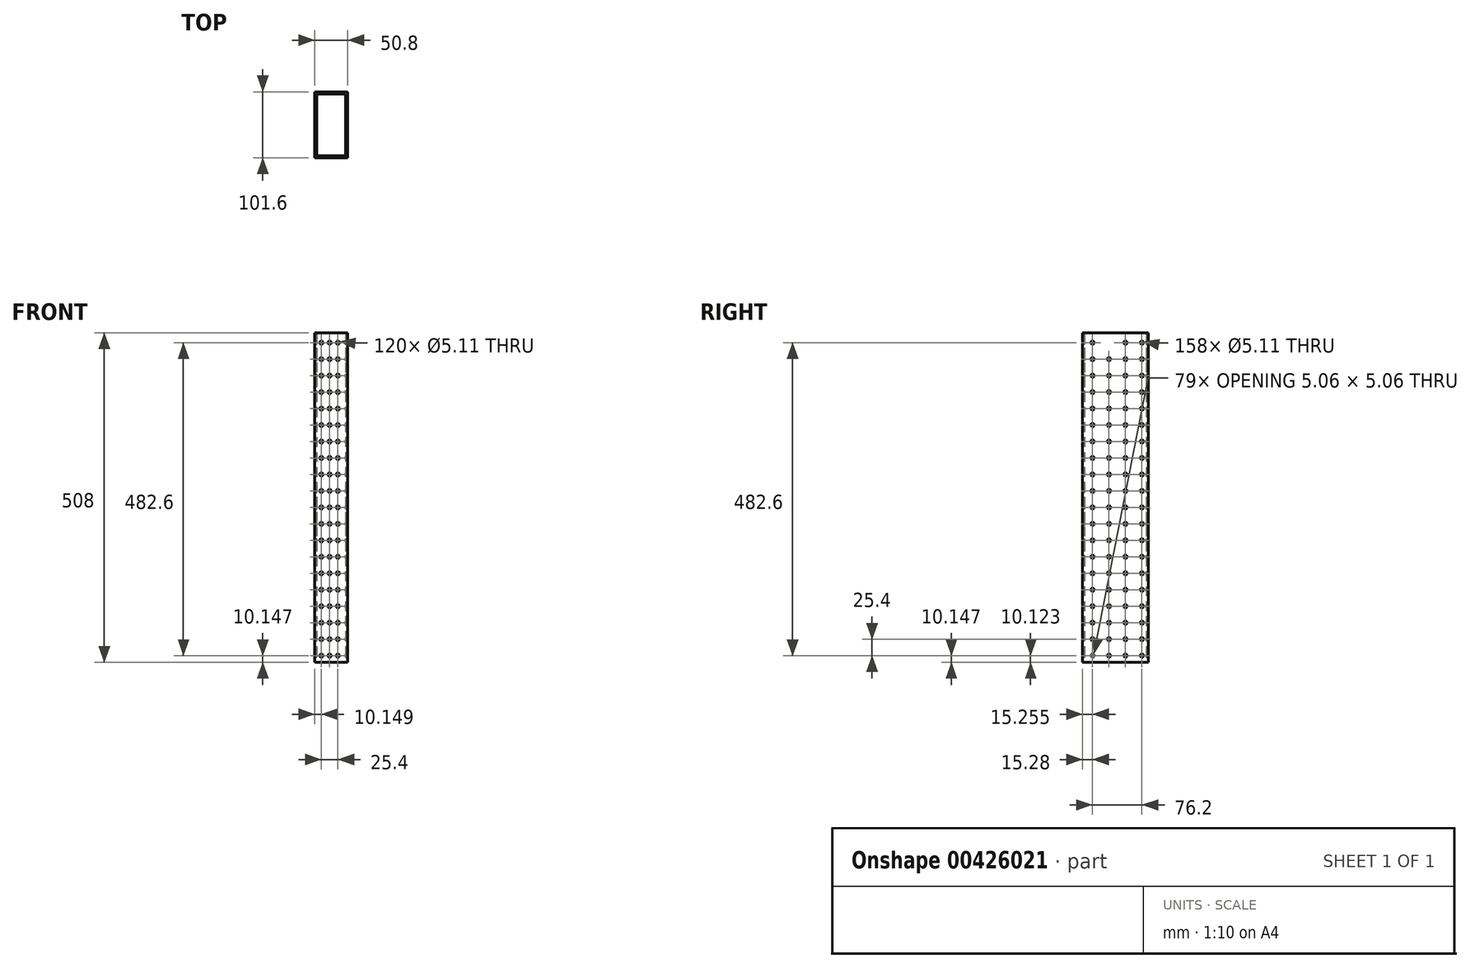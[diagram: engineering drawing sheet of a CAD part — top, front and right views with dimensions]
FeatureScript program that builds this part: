
annotation { "Feature Type Name" : "Feature", "Feature Type Description" : "" }
export const myFeature = defineFeature(function(context is Context, id is Id, definition is map)
    precondition{}
    {
        {
            var Q0;
            Q0=qCreatedBy(makeId("Top.planeOp"),FACE);
            var sketch = newSketch(context, id + "F0", { "sketchPlane" : qUnion([Q0])});
            skLineSegment(sketch, "E0.bottom", {"start": v(-26.2, 70.95) * mm, "end": v(24.6, 70.95) * mm});
            skLineSegment(sketch, "E0.top", {"start": v(-26.2, -30.65) * mm, "end": v(24.6, -30.65) * mm});
            skLineSegment(sketch, "E0.left", {"start": v(-26.2, 70.95) * mm, "end": v(-26.2, -30.65) * mm});
            skLineSegment(sketch, "E0.right", {"start": v(24.6, 70.95) * mm, "end": v(24.6, -30.65) * mm});
            skLineSegment(sketch, "E1.bottom", {"start": v(21.42, 67.78) * mm, "end": v(-23.03, 67.78) * mm});
            skLineSegment(sketch, "E1.top", {"start": v(21.42, -27.47) * mm, "end": v(-23.03, -27.47) * mm});
            skLineSegment(sketch, "E1.left", {"start": v(21.42, 67.78) * mm, "end": v(21.42, -27.47) * mm});
            skLineSegment(sketch, "E1.right", {"start": v(-23.03, 67.78) * mm, "end": v(-23.03, -27.47) * mm});
            skSolve(sketch);
        }
        {
            var Q0;
            Q0 = qSketchRegion(id + "F0", true);
            extrude(context, id + "F1", {"entities" : qUnion([Q0]), "depth" : 508 * mm});
        }
        {
            var Q0;
            Q0=makeQuery(id+"F1.opExtrude","SWEPT_FACE",FACE,{"disambiguationData":[OSD([sQuery(id+"F0.wireOp",EDGE,"E0.right")])]});
            var sketch = newSketch(context, id + "F2", { "sketchPlane" : qUnion([Q0])});
            skCircle(sketch, "E2", {"center": v(-15.4, 492.75) * mm, "radius": 2.55 * mm});
            skCircle(sketch, "E3.1.0.0", {"center": v(10, 492.75) * mm, "radius": 2.55 * mm});
            skCircle(sketch, "E3.2.0.0", {"center": v(35.4, 492.75) * mm, "radius": 2.55 * mm});
            skCircle(sketch, "E3.3.0.0", {"center": v(60.8, 492.75) * mm, "radius": 2.55 * mm});
            skLineSegment(sketch, "E3.direction1", {"start": v(-15.4, 492.75) * mm, "end": v(10, 492.75) * mm, "construction": true});
            skCircle(sketch, "E4.0.1.0", {"center": v(-15.4, 467.35) * mm, "radius": 2.55 * mm});
            skCircle(sketch, "E4.0.2.0", {"center": v(-15.4, 441.95) * mm, "radius": 2.55 * mm});
            skCircle(sketch, "E4.0.3.0", {"center": v(-15.4, 416.55) * mm, "radius": 2.55 * mm});
            skCircle(sketch, "E4.0.4.0", {"center": v(-15.4, 391.15) * mm, "radius": 2.55 * mm});
            skCircle(sketch, "E4.0.5.0", {"center": v(-15.4, 365.75) * mm, "radius": 2.55 * mm});
            skCircle(sketch, "E4.0.6.0", {"center": v(-15.4, 340.35) * mm, "radius": 2.55 * mm});
            skCircle(sketch, "E4.0.7.0", {"center": v(-15.4, 314.95) * mm, "radius": 2.55 * mm});
            skCircle(sketch, "E4.0.8.0", {"center": v(-15.4, 289.55) * mm, "radius": 2.55 * mm});
            skCircle(sketch, "E4.0.9.0", {"center": v(-15.4, 264.15) * mm, "radius": 2.55 * mm});
            skCircle(sketch, "E4.0.10.0", {"center": v(-15.4, 238.75) * mm, "radius": 2.55 * mm});
            skCircle(sketch, "E4.0.11.0", {"center": v(-15.4, 213.35) * mm, "radius": 2.55 * mm});
            skCircle(sketch, "E4.0.12.0", {"center": v(-15.4, 187.95) * mm, "radius": 2.55 * mm});
            skCircle(sketch, "E4.0.13.0", {"center": v(-15.4, 162.55) * mm, "radius": 2.55 * mm});
            skCircle(sketch, "E4.0.14.0", {"center": v(-15.4, 137.15) * mm, "radius": 2.55 * mm});
            skCircle(sketch, "E4.0.15.0", {"center": v(-15.4, 111.75) * mm, "radius": 2.55 * mm});
            skCircle(sketch, "E4.0.16.0", {"center": v(-15.4, 86.35) * mm, "radius": 2.55 * mm});
            skCircle(sketch, "E4.0.17.0", {"center": v(-15.4, 60.95) * mm, "radius": 2.55 * mm});
            skCircle(sketch, "E4.0.18.0", {"center": v(-15.4, 35.55) * mm, "radius": 2.55 * mm});
            skCircle(sketch, "E4.0.19.0", {"center": v(-15.4, 10.15) * mm, "radius": 2.55 * mm});
            skCircle(sketch, "E4.1.1.0", {"center": v(10, 467.35) * mm, "radius": 2.55 * mm});
            skCircle(sketch, "E4.1.2.0", {"center": v(10, 441.95) * mm, "radius": 2.55 * mm});
            skCircle(sketch, "E4.1.3.0", {"center": v(10, 416.55) * mm, "radius": 2.55 * mm});
            skCircle(sketch, "E4.1.4.0", {"center": v(10, 391.15) * mm, "radius": 2.55 * mm});
            skCircle(sketch, "E4.1.5.0", {"center": v(10, 365.75) * mm, "radius": 2.55 * mm});
            skCircle(sketch, "E4.1.6.0", {"center": v(10, 340.35) * mm, "radius": 2.55 * mm});
            skCircle(sketch, "E4.1.7.0", {"center": v(10, 314.95) * mm, "radius": 2.55 * mm});
            skCircle(sketch, "E4.1.8.0", {"center": v(10, 289.55) * mm, "radius": 2.55 * mm});
            skCircle(sketch, "E4.1.9.0", {"center": v(10, 264.15) * mm, "radius": 2.55 * mm});
            skCircle(sketch, "E4.1.10.0", {"center": v(10, 238.75) * mm, "radius": 2.55 * mm});
            skCircle(sketch, "E4.1.11.0", {"center": v(10, 213.35) * mm, "radius": 2.55 * mm});
            skCircle(sketch, "E4.1.12.0", {"center": v(10, 187.95) * mm, "radius": 2.55 * mm});
            skCircle(sketch, "E4.1.13.0", {"center": v(10, 162.55) * mm, "radius": 2.55 * mm});
            skCircle(sketch, "E4.1.14.0", {"center": v(10, 137.15) * mm, "radius": 2.55 * mm});
            skCircle(sketch, "E4.1.15.0", {"center": v(10, 111.75) * mm, "radius": 2.55 * mm});
            skCircle(sketch, "E4.1.16.0", {"center": v(10, 86.35) * mm, "radius": 2.55 * mm});
            skCircle(sketch, "E4.1.17.0", {"center": v(10, 60.95) * mm, "radius": 2.55 * mm});
            skCircle(sketch, "E4.1.18.0", {"center": v(10, 35.55) * mm, "radius": 2.55 * mm});
            skCircle(sketch, "E4.1.19.0", {"center": v(10, 10.15) * mm, "radius": 2.55 * mm});
            skCircle(sketch, "E4.2.1.0", {"center": v(35.4, 467.35) * mm, "radius": 2.55 * mm});
            skCircle(sketch, "E4.2.2.0", {"center": v(35.4, 441.95) * mm, "radius": 2.55 * mm});
            skCircle(sketch, "E4.2.3.0", {"center": v(35.4, 416.55) * mm, "radius": 2.55 * mm});
            skCircle(sketch, "E4.2.4.0", {"center": v(35.4, 391.15) * mm, "radius": 2.55 * mm});
            skCircle(sketch, "E4.2.5.0", {"center": v(35.4, 365.75) * mm, "radius": 2.55 * mm});
            skCircle(sketch, "E4.2.6.0", {"center": v(35.4, 340.35) * mm, "radius": 2.55 * mm});
            skCircle(sketch, "E4.2.7.0", {"center": v(35.4, 314.95) * mm, "radius": 2.55 * mm});
            skCircle(sketch, "E4.2.8.0", {"center": v(35.4, 289.55) * mm, "radius": 2.55 * mm});
            skCircle(sketch, "E4.2.9.0", {"center": v(35.4, 264.15) * mm, "radius": 2.55 * mm});
            skCircle(sketch, "E4.2.10.0", {"center": v(35.4, 238.75) * mm, "radius": 2.55 * mm});
            skCircle(sketch, "E4.2.11.0", {"center": v(35.4, 213.35) * mm, "radius": 2.55 * mm});
            skCircle(sketch, "E4.2.12.0", {"center": v(35.4, 187.95) * mm, "radius": 2.55 * mm});
            skCircle(sketch, "E4.2.13.0", {"center": v(35.4, 162.55) * mm, "radius": 2.55 * mm});
            skCircle(sketch, "E4.2.14.0", {"center": v(35.4, 137.15) * mm, "radius": 2.55 * mm});
            skCircle(sketch, "E4.2.15.0", {"center": v(35.4, 111.75) * mm, "radius": 2.55 * mm});
            skCircle(sketch, "E4.2.16.0", {"center": v(35.4, 86.35) * mm, "radius": 2.55 * mm});
            skCircle(sketch, "E4.2.17.0", {"center": v(35.4, 60.95) * mm, "radius": 2.55 * mm});
            skCircle(sketch, "E4.2.18.0", {"center": v(35.4, 35.55) * mm, "radius": 2.55 * mm});
            skCircle(sketch, "E4.2.19.0", {"center": v(35.4, 10.15) * mm, "radius": 2.55 * mm});
            skLineSegment(sketch, "E4.direction2", {"start": v(-15.4, 492.75) * mm, "end": v(-15.4, 467.35) * mm, "construction": true});
            skCircle(sketch, "E5.0.3.1", {"center": v(60.8, 467.35) * mm, "radius": 2.55 * mm});
            skCircle(sketch, "E5.0.3.2", {"center": v(60.8, 441.95) * mm, "radius": 2.55 * mm});
            skCircle(sketch, "E5.0.3.3", {"center": v(60.8, 416.55) * mm, "radius": 2.55 * mm});
            skCircle(sketch, "E5.0.3.4", {"center": v(60.8, 391.15) * mm, "radius": 2.55 * mm});
            skCircle(sketch, "E5.0.3.5", {"center": v(60.8, 365.75) * mm, "radius": 2.55 * mm});
            skCircle(sketch, "E5.0.3.6", {"center": v(60.8, 340.35) * mm, "radius": 2.55 * mm});
            skCircle(sketch, "E5.0.3.7", {"center": v(60.8, 314.95) * mm, "radius": 2.55 * mm});
            skCircle(sketch, "E5.0.3.8", {"center": v(60.8, 289.55) * mm, "radius": 2.55 * mm});
            skCircle(sketch, "E5.0.3.9", {"center": v(60.8, 264.15) * mm, "radius": 2.55 * mm});
            skCircle(sketch, "E5.0.3.10", {"center": v(60.8, 238.75) * mm, "radius": 2.55 * mm});
            skCircle(sketch, "E5.0.3.11", {"center": v(60.8, 213.35) * mm, "radius": 2.55 * mm});
            skCircle(sketch, "E5.0.3.12", {"center": v(60.8, 187.95) * mm, "radius": 2.55 * mm});
            skCircle(sketch, "E5.0.3.13", {"center": v(60.8, 162.55) * mm, "radius": 2.55 * mm});
            skCircle(sketch, "E5.0.3.14", {"center": v(60.8, 137.15) * mm, "radius": 2.55 * mm});
            skCircle(sketch, "E5.0.3.15", {"center": v(60.8, 111.75) * mm, "radius": 2.55 * mm});
            skCircle(sketch, "E5.0.3.16", {"center": v(60.8, 86.35) * mm, "radius": 2.55 * mm});
            skCircle(sketch, "E5.0.3.17", {"center": v(60.8, 60.95) * mm, "radius": 2.55 * mm});
            skCircle(sketch, "E5.0.3.18", {"center": v(60.8, 35.55) * mm, "radius": 2.55 * mm});
            skCircle(sketch, "E5.0.3.19", {"center": v(60.8, 10.15) * mm, "radius": 2.55 * mm});
            skSolve(sketch);
        }
        {
            var Q0;
            Q0=sQuery(id+"F2.wireOp",VERTEX,"E4.1.18.0.center");
            var Q1;
            Q1=sQuery(id+"F2.wireOp",VERTEX,"E5.0.3.1.center");
            var Q2;
            Q2=sQuery(id+"F2.wireOp",VERTEX,"E5.0.3.17.center");
            var Q3;
            Q3=sQuery(id+"F2.wireOp",VERTEX,"E5.0.3.10.center");
            var Q4;
            Q4=sQuery(id+"F2.wireOp",VERTEX,"E4.1.2.0.center");
            var Q5;
            Q5=sQuery(id+"F2.wireOp",VERTEX,"E4.1.9.0.center");
            var Q6;
            Q6=sQuery(id+"F2.wireOp",VERTEX,"E4.2.5.0.center");
            var Q7;
            Q7=sQuery(id+"F2.wireOp",VERTEX,"E4.2.14.0.center");
            var Q8;
            Q8=sQuery(id+"F2.wireOp",VERTEX,"E4.0.7.0.center");
            var Q9;
            Q9=sQuery(id+"F2.wireOp",VERTEX,"E5.0.3.18.center");
            var Q10;
            Q10=sQuery(id+"F2.wireOp",VERTEX,"E5.0.3.2.center");
            var Q11;
            Q11=sQuery(id+"F2.wireOp",VERTEX,"E5.0.3.11.center");
            var Q12;
            Q12=sQuery(id+"F2.wireOp",VERTEX,"E4.2.15.0.center");
            var Q13;
            Q13=sQuery(id+"F2.wireOp",VERTEX,"E4.1.19.0.center");
            var Q14;
            Q14=sQuery(id+"F2.wireOp",VERTEX,"E4.1.3.0.center");
            var Q15;
            Q15=sQuery(id+"F2.wireOp",VERTEX,"E4.2.6.0.center");
            var Q16;
            Q16=sQuery(id+"F2.wireOp",VERTEX,"E4.1.10.0.center");
            var Q17;
            Q17=sQuery(id+"F2.wireOp",VERTEX,"E4.0.14.0.center");
            var Q18;
            Q18=sQuery(id+"F2.wireOp",VERTEX,"E4.0.8.0.center");
            var Q19;
            Q19=sQuery(id+"F2.wireOp",VERTEX,"E5.0.3.12.center");
            var Q20;
            Q20=sQuery(id+"F2.wireOp",VERTEX,"E4.2.16.0.center");
            var Q21;
            Q21=sQuery(id+"F2.wireOp",VERTEX,"E4.1.4.0.center");
            var Q22;
            Q22=sQuery(id+"F2.wireOp",VERTEX,"E4.2.7.0.center");
            var Q23;
            Q23=sQuery(id+"F2.wireOp",VERTEX,"E4.1.11.0.center");
            var Q24;
            Q24=sQuery(id+"F2.wireOp",VERTEX,"E4.0.15.0.center");
            var Q25;
            Q25=sQuery(id+"F2.wireOp",VERTEX,"E5.0.3.19.center");
            var Q26;
            Q26=sQuery(id+"F2.wireOp",VERTEX,"E5.0.3.3.center");
            var Q27;
            Q27=sQuery(id+"F2.wireOp",VERTEX,"E4.0.4.0.center");
            var Q28;
            Q28=sQuery(id+"F2.wireOp",VERTEX,"E4.0.9.0.center");
            var Q29;
            Q29=sQuery(id+"F2.wireOp",VERTEX,"E4.0.5.0.center");
            var Q30;
            Q30=sQuery(id+"F2.wireOp",VERTEX,"E5.0.3.13.center");
            var Q31;
            Q31=sQuery(id+"F2.wireOp",VERTEX,"E4.0.6.0.center");
            var Q32;
            Q32=sQuery(id+"F2.wireOp",VERTEX,"E4.2.17.0.center");
            var Q33;
            Q33=sQuery(id+"F2.wireOp",VERTEX,"E4.2.1.0.center");
            var Q34;
            Q34=sQuery(id+"F2.wireOp",VERTEX,"E4.1.5.0.center");
            var Q35;
            Q35=sQuery(id+"F2.wireOp",VERTEX,"E2.center");
            var Q36;
            Q36=sQuery(id+"F2.wireOp",VERTEX,"E3.2.0.0.center");
            var Q37;
            Q37=sQuery(id+"F2.wireOp",VERTEX,"E3.3.0.0.center");
            var Q38;
            Q38=sQuery(id+"F2.wireOp",VERTEX,"E4.0.1.0.center");
            var Q39;
            Q39=sQuery(id+"F2.wireOp",VERTEX,"E4.0.2.0.center");
            var Q40;
            Q40=sQuery(id+"F2.wireOp",VERTEX,"E4.0.3.0.center");
            var Q41;
            Q41=sQuery(id+"F2.wireOp",VERTEX,"E4.2.8.0.center");
            var Q42;
            Q42=sQuery(id+"F2.wireOp",VERTEX,"E4.1.12.0.center");
            var Q43;
            Q43=sQuery(id+"F2.wireOp",VERTEX,"E4.0.16.0.center");
            var Q44;
            Q44=sQuery(id+"F2.wireOp",VERTEX,"E5.0.3.4.center");
            var Q45;
            Q45=sQuery(id+"F2.wireOp",VERTEX,"E4.0.10.0.center");
            var Q46;
            Q46=sQuery(id+"F2.wireOp",VERTEX,"E5.0.3.14.center");
            var Q47;
            Q47=sQuery(id+"F2.wireOp",VERTEX,"E4.2.18.0.center");
            var Q48;
            Q48=sQuery(id+"F2.wireOp",VERTEX,"E4.2.2.0.center");
            var Q49;
            Q49=sQuery(id+"F2.wireOp",VERTEX,"E4.1.6.0.center");
            var Q50;
            Q50=sQuery(id+"F2.wireOp",VERTEX,"E4.2.9.0.center");
            var Q51;
            Q51=sQuery(id+"F2.wireOp",VERTEX,"E4.1.13.0.center");
            var Q52;
            Q52=sQuery(id+"F2.wireOp",VERTEX,"E4.0.17.0.center");
            var Q53;
            Q53=sQuery(id+"F2.wireOp",VERTEX,"E5.0.3.5.center");
            var Q54;
            Q54=sQuery(id+"F2.wireOp",VERTEX,"E4.0.11.0.center");
            var Q55;
            Q55=sQuery(id+"F2.wireOp",VERTEX,"E5.0.3.15.center");
            var Q56;
            Q56=sQuery(id+"F2.wireOp",VERTEX,"E5.0.3.8.center");
            var Q57;
            Q57=sQuery(id+"F2.wireOp",VERTEX,"E4.2.19.0.center");
            var Q58;
            Q58=sQuery(id+"F2.wireOp",VERTEX,"E4.2.12.0.center");
            var Q59;
            Q59=sQuery(id+"F2.wireOp",VERTEX,"E4.1.16.0.center");
            var Q60;
            Q60=sQuery(id+"F2.wireOp",VERTEX,"E4.2.3.0.center");
            var Q61;
            Q61=sQuery(id+"F2.wireOp",VERTEX,"E3.1.0.0.center");
            var Q62;
            Q62=sQuery(id+"F2.wireOp",VERTEX,"E4.1.7.0.center");
            var Q63;
            Q63=sQuery(id+"F2.wireOp",VERTEX,"E4.0.13.0.center");
            var Q64;
            Q64=sQuery(id+"F2.wireOp",VERTEX,"E5.0.3.7.center");
            var Q65;
            Q65=sQuery(id+"F2.wireOp",VERTEX,"E4.0.19.0.center");
            var Q66;
            Q66=sQuery(id+"F2.wireOp",VERTEX,"E4.1.15.0.center");
            var Q67;
            Q67=sQuery(id+"F2.wireOp",VERTEX,"E4.2.11.0.center");
            var Q68;
            Q68=sQuery(id+"F2.wireOp",VERTEX,"E4.1.1.0.center");
            var Q69;
            Q69=sQuery(id+"F2.wireOp",VERTEX,"E4.1.8.0.center");
            var Q70;
            Q70=sQuery(id+"F2.wireOp",VERTEX,"E4.1.17.0.center");
            var Q71;
            Q71=sQuery(id+"F2.wireOp",VERTEX,"E4.2.4.0.center");
            var Q72;
            Q72=sQuery(id+"F2.wireOp",VERTEX,"E4.2.13.0.center");
            var Q73;
            Q73=sQuery(id+"F2.wireOp",VERTEX,"E5.0.3.9.center");
            var Q74;
            Q74=sQuery(id+"F2.wireOp",VERTEX,"E5.0.3.16.center");
            var Q75;
            Q75=sQuery(id+"F2.wireOp",VERTEX,"E4.0.12.0.center");
            var Q76;
            Q76=sQuery(id+"F2.wireOp",VERTEX,"E5.0.3.6.center");
            var Q77;
            Q77=sQuery(id+"F2.wireOp",VERTEX,"E4.0.18.0.center");
            var Q78;
            Q78=sQuery(id+"F2.wireOp",VERTEX,"E4.1.14.0.center");
            var Q79;
            Q79=sQuery(id+"F2.wireOp",VERTEX,"E4.2.10.0.center");
            var Q80;
            Q80=makeQuery(id+"F1.opExtrude","SWEPT_BODY",BODY,{"disambiguationData":[OSD([sQuery(id+"F0.wireOp",EDGE,"E0.bottom"),sQuery(id+"F0.wireOp",EDGE,"E0.top"),sQuery(id+"F0.wireOp",EDGE,"E0.left"),sQuery(id+"F0.wireOp",EDGE,"E0.right"),sQuery(id+"F0.wireOp",EDGE,"E1.bottom"),sQuery(id+"F0.wireOp",EDGE,"E1.top"),sQuery(id+"F0.wireOp",EDGE,"E1.left"),sQuery(id+"F0.wireOp",EDGE,"E1.right")])]});
            hole(context, id + "F3", {"style" : HoleStyle.SIMPLE, "endStyle" : HoleEndStyle.THROUGH, "holeDiameter" : 5.1 * mm, "isTappedThrough" : true, "tappedDepth" : 12.7 * mm, "tapClearance" : 3, "locations" : qUnion([Q0, Q1, Q2, Q3, Q4, Q5, Q6, Q7, Q8, Q9, Q10, Q11, Q12, Q13, Q14, Q15, Q16, Q17, Q18, Q19, Q20, Q21, Q22, Q23, Q24, Q25, Q26, Q27, Q28, Q29, Q30, Q31, Q32, Q33, Q34, Q35, Q36, Q37, Q38, Q39, Q40, Q41, Q42, Q43, Q44, Q45, Q46, Q47, Q48, Q49, Q50, Q51, Q52, Q53, Q54, Q55, Q56, Q57, Q58, Q59, Q60, Q61, Q62, Q63, Q64, Q65, Q66, Q67, Q68, Q69, Q70, Q71, Q72, Q73, Q74, Q75, Q76, Q77, Q78, Q79]), "scope" : qUnion([Q80])});
        }
        {
            var Q0;
            Q0=makeQuery(id+"F1.opExtrude","SWEPT_FACE",FACE,{"disambiguationData":[OSD([sQuery(id+"F0.wireOp",EDGE,"E0.bottom")])]});
            var sketch = newSketch(context, id + "F4", { "sketchPlane" : qUnion([Q0])});
            skCircle(sketch, "E6", {"center": v(-9.34, 492.75) * mm, "radius": 2.55 * mm});
            skCircle(sketch, "E7.0.1.0", {"center": v(-9.34, 467.35) * mm, "radius": 2.55 * mm});
            skCircle(sketch, "E7.0.2.0", {"center": v(-9.34, 441.95) * mm, "radius": 2.55 * mm});
            skCircle(sketch, "E7.0.3.0", {"center": v(-9.34, 416.55) * mm, "radius": 2.55 * mm});
            skCircle(sketch, "E7.0.4.0", {"center": v(-9.34, 391.15) * mm, "radius": 2.55 * mm});
            skCircle(sketch, "E7.0.5.0", {"center": v(-9.34, 365.75) * mm, "radius": 2.55 * mm});
            skCircle(sketch, "E7.0.6.0", {"center": v(-9.34, 340.35) * mm, "radius": 2.55 * mm});
            skCircle(sketch, "E7.0.7.0", {"center": v(-9.34, 314.95) * mm, "radius": 2.55 * mm});
            skCircle(sketch, "E7.0.8.0", {"center": v(-9.34, 289.55) * mm, "radius": 2.55 * mm});
            skCircle(sketch, "E7.0.9.0", {"center": v(-9.34, 264.15) * mm, "radius": 2.55 * mm});
            skCircle(sketch, "E7.0.10.0", {"center": v(-9.34, 238.75) * mm, "radius": 2.55 * mm});
            skCircle(sketch, "E7.0.11.0", {"center": v(-9.34, 213.35) * mm, "radius": 2.55 * mm});
            skCircle(sketch, "E7.0.12.0", {"center": v(-9.34, 187.95) * mm, "radius": 2.55 * mm});
            skCircle(sketch, "E7.0.13.0", {"center": v(-9.34, 162.55) * mm, "radius": 2.55 * mm});
            skCircle(sketch, "E7.0.14.0", {"center": v(-9.34, 137.15) * mm, "radius": 2.55 * mm});
            skCircle(sketch, "E7.0.15.0", {"center": v(-9.34, 111.75) * mm, "radius": 2.55 * mm});
            skCircle(sketch, "E7.0.16.0", {"center": v(-9.34, 86.35) * mm, "radius": 2.55 * mm});
            skCircle(sketch, "E7.0.17.0", {"center": v(-9.34, 60.95) * mm, "radius": 2.55 * mm});
            skCircle(sketch, "E7.0.18.0", {"center": v(-9.34, 35.55) * mm, "radius": 2.55 * mm});
            skCircle(sketch, "E7.0.19.0", {"center": v(-9.34, 10.15) * mm, "radius": 2.55 * mm});
            skCircle(sketch, "E7.1.0.0", {"center": v(3.36, 492.75) * mm, "radius": 2.55 * mm});
            skCircle(sketch, "E7.1.1.0", {"center": v(3.36, 467.35) * mm, "radius": 2.55 * mm});
            skCircle(sketch, "E7.1.2.0", {"center": v(3.36, 441.95) * mm, "radius": 2.55 * mm});
            skCircle(sketch, "E7.1.3.0", {"center": v(3.36, 416.55) * mm, "radius": 2.55 * mm});
            skCircle(sketch, "E7.1.4.0", {"center": v(3.36, 391.15) * mm, "radius": 2.55 * mm});
            skCircle(sketch, "E7.1.5.0", {"center": v(3.36, 365.75) * mm, "radius": 2.55 * mm});
            skCircle(sketch, "E7.1.6.0", {"center": v(3.36, 340.35) * mm, "radius": 2.55 * mm});
            skCircle(sketch, "E7.1.7.0", {"center": v(3.36, 314.95) * mm, "radius": 2.55 * mm});
            skCircle(sketch, "E7.1.8.0", {"center": v(3.36, 289.55) * mm, "radius": 2.55 * mm});
            skCircle(sketch, "E7.1.9.0", {"center": v(3.36, 264.15) * mm, "radius": 2.55 * mm});
            skCircle(sketch, "E7.1.10.0", {"center": v(3.36, 238.75) * mm, "radius": 2.55 * mm});
            skCircle(sketch, "E7.1.11.0", {"center": v(3.36, 213.35) * mm, "radius": 2.55 * mm});
            skCircle(sketch, "E7.1.12.0", {"center": v(3.36, 187.95) * mm, "radius": 2.55 * mm});
            skCircle(sketch, "E7.1.13.0", {"center": v(3.36, 162.55) * mm, "radius": 2.55 * mm});
            skCircle(sketch, "E7.1.14.0", {"center": v(3.36, 137.15) * mm, "radius": 2.55 * mm});
            skCircle(sketch, "E7.1.15.0", {"center": v(3.36, 111.75) * mm, "radius": 2.55 * mm});
            skCircle(sketch, "E7.1.16.0", {"center": v(3.36, 86.35) * mm, "radius": 2.55 * mm});
            skCircle(sketch, "E7.1.17.0", {"center": v(3.36, 60.95) * mm, "radius": 2.55 * mm});
            skCircle(sketch, "E7.1.18.0", {"center": v(3.36, 35.55) * mm, "radius": 2.55 * mm});
            skCircle(sketch, "E7.1.19.0", {"center": v(3.36, 10.15) * mm, "radius": 2.55 * mm});
            skCircle(sketch, "E7.2.0.0", {"center": v(16.06, 492.75) * mm, "radius": 2.55 * mm});
            skCircle(sketch, "E7.2.1.0", {"center": v(16.06, 467.35) * mm, "radius": 2.55 * mm});
            skCircle(sketch, "E7.2.2.0", {"center": v(16.06, 441.95) * mm, "radius": 2.55 * mm});
            skCircle(sketch, "E7.2.3.0", {"center": v(16.06, 416.55) * mm, "radius": 2.55 * mm});
            skCircle(sketch, "E7.2.4.0", {"center": v(16.06, 391.15) * mm, "radius": 2.55 * mm});
            skCircle(sketch, "E7.2.5.0", {"center": v(16.06, 365.75) * mm, "radius": 2.55 * mm});
            skCircle(sketch, "E7.2.6.0", {"center": v(16.06, 340.35) * mm, "radius": 2.55 * mm});
            skCircle(sketch, "E7.2.7.0", {"center": v(16.06, 314.95) * mm, "radius": 2.55 * mm});
            skCircle(sketch, "E7.2.8.0", {"center": v(16.06, 289.55) * mm, "radius": 2.55 * mm});
            skCircle(sketch, "E7.2.9.0", {"center": v(16.06, 264.15) * mm, "radius": 2.55 * mm});
            skCircle(sketch, "E7.2.10.0", {"center": v(16.06, 238.75) * mm, "radius": 2.55 * mm});
            skCircle(sketch, "E7.2.11.0", {"center": v(16.06, 213.35) * mm, "radius": 2.55 * mm});
            skCircle(sketch, "E7.2.12.0", {"center": v(16.06, 187.95) * mm, "radius": 2.55 * mm});
            skCircle(sketch, "E7.2.13.0", {"center": v(16.06, 162.55) * mm, "radius": 2.55 * mm});
            skCircle(sketch, "E7.2.14.0", {"center": v(16.06, 137.15) * mm, "radius": 2.55 * mm});
            skCircle(sketch, "E7.2.15.0", {"center": v(16.06, 111.75) * mm, "radius": 2.55 * mm});
            skCircle(sketch, "E7.2.16.0", {"center": v(16.06, 86.35) * mm, "radius": 2.55 * mm});
            skCircle(sketch, "E7.2.17.0", {"center": v(16.06, 60.95) * mm, "radius": 2.55 * mm});
            skCircle(sketch, "E7.2.18.0", {"center": v(16.06, 35.55) * mm, "radius": 2.55 * mm});
            skCircle(sketch, "E7.2.19.0", {"center": v(16.06, 10.15) * mm, "radius": 2.55 * mm});
            skLineSegment(sketch, "E7.direction1", {"start": v(-9.34, 492.75) * mm, "end": v(3.36, 492.75) * mm, "construction": true});
            skLineSegment(sketch, "E7.direction2", {"start": v(-9.34, 492.75) * mm, "end": v(-9.34, 467.35) * mm, "construction": true});
            skSolve(sketch);
        }
        {
            var Q0;
            Q0=sQuery(id+"F4.wireOp",VERTEX,"E7.2.10.0.center");
            var Q1;
            Q1=sQuery(id+"F4.wireOp",VERTEX,"E7.0.18.0.center");
            var Q2;
            Q2=sQuery(id+"F4.wireOp",VERTEX,"E7.1.14.0.center");
            var Q3;
            Q3=sQuery(id+"F4.wireOp",VERTEX,"E7.2.11.0.center");
            var Q4;
            Q4=sQuery(id+"F4.wireOp",VERTEX,"E7.0.19.0.center");
            var Q5;
            Q5=sQuery(id+"F4.wireOp",VERTEX,"E7.1.15.0.center");
            var Q6;
            Q6=sQuery(id+"F4.wireOp",VERTEX,"E7.2.13.0.center");
            var Q7;
            Q7=sQuery(id+"F4.wireOp",VERTEX,"E7.1.1.0.center");
            var Q8;
            Q8=sQuery(id+"F4.wireOp",VERTEX,"E7.1.17.0.center");
            var Q9;
            Q9=sQuery(id+"F4.wireOp",VERTEX,"E7.2.12.0.center");
            var Q10;
            Q10=sQuery(id+"F4.wireOp",VERTEX,"E7.1.16.0.center");
            var Q11;
            Q11=sQuery(id+"F4.wireOp",VERTEX,"E7.2.15.0.center");
            var Q12;
            Q12=sQuery(id+"F4.wireOp",VERTEX,"E7.1.3.0.center");
            var Q13;
            Q13=sQuery(id+"F4.wireOp",VERTEX,"E7.1.19.0.center");
            var Q14;
            Q14=sQuery(id+"F4.wireOp",VERTEX,"E7.0.11.0.center");
            var Q15;
            Q15=sQuery(id+"F4.wireOp",VERTEX,"E7.direction1.end");
            var Q16;
            Q16=sQuery(id+"F4.wireOp",VERTEX,"E7.2.2.0.center");
            var Q17;
            Q17=sQuery(id+"F4.wireOp",VERTEX,"E7.2.18.0.center");
            var Q18;
            Q18=sQuery(id+"F4.wireOp",VERTEX,"E7.1.6.0.center");
            var Q19;
            Q19=sQuery(id+"F4.wireOp",VERTEX,"E7.0.1.0.center");
            var Q20;
            Q20=sQuery(id+"F4.wireOp",VERTEX,"E7.0.10.0.center");
            var Q21;
            Q21=sQuery(id+"F4.wireOp",VERTEX,"E7.0.9.0.center");
            var Q22;
            Q22=sQuery(id+"F4.wireOp",VERTEX,"E7.0.2.0.center");
            var Q23;
            Q23=sQuery(id+"F4.wireOp",VERTEX,"E7.0.4.0.center");
            var Q24;
            Q24=sQuery(id+"F4.wireOp",VERTEX,"E7.0.3.0.center");
            var Q25;
            Q25=sQuery(id+"F4.wireOp",VERTEX,"E7.2.14.0.center");
            var Q26;
            Q26=sQuery(id+"F4.wireOp",VERTEX,"E7.0.6.0.center");
            var Q27;
            Q27=sQuery(id+"F4.wireOp",VERTEX,"E7.1.2.0.center");
            var Q28;
            Q28=sQuery(id+"F4.wireOp",VERTEX,"E7.1.18.0.center");
            var Q29;
            Q29=sQuery(id+"F4.wireOp",VERTEX,"E7.0.5.0.center");
            var Q30;
            Q30=sQuery(id+"F4.wireOp",VERTEX,"E7.0.8.0.center");
            var Q31;
            Q31=sQuery(id+"F4.wireOp",VERTEX,"E7.0.7.0.center");
            var Q32;
            Q32=sQuery(id+"F4.wireOp",VERTEX,"E7.2.1.0.center");
            var Q33;
            Q33=sQuery(id+"F4.wireOp",VERTEX,"E7.2.17.0.center");
            var Q34;
            Q34=sQuery(id+"F4.wireOp",VERTEX,"E7.1.5.0.center");
            var Q35;
            Q35=sQuery(id+"F4.wireOp",VERTEX,"E7.direction1.start");
            var Q36;
            Q36=sQuery(id+"F4.wireOp",VERTEX,"E7.2.16.0.center");
            var Q37;
            Q37=sQuery(id+"F4.wireOp",VERTEX,"E7.1.4.0.center");
            var Q38;
            Q38=sQuery(id+"F4.wireOp",VERTEX,"E7.2.0.0.center");
            var Q39;
            Q39=sQuery(id+"F4.wireOp",VERTEX,"E7.2.3.0.center");
            var Q40;
            Q40=sQuery(id+"F4.wireOp",VERTEX,"E7.2.19.0.center");
            var Q41;
            Q41=sQuery(id+"F4.wireOp",VERTEX,"E7.1.7.0.center");
            var Q42;
            Q42=sQuery(id+"F4.wireOp",VERTEX,"E7.2.5.0.center");
            var Q43;
            Q43=sQuery(id+"F4.wireOp",VERTEX,"E7.0.13.0.center");
            var Q44;
            Q44=sQuery(id+"F4.wireOp",VERTEX,"E7.1.9.0.center");
            var Q45;
            Q45=sQuery(id+"F4.wireOp",VERTEX,"E7.2.4.0.center");
            var Q46;
            Q46=sQuery(id+"F4.wireOp",VERTEX,"E7.0.12.0.center");
            var Q47;
            Q47=sQuery(id+"F4.wireOp",VERTEX,"E7.1.8.0.center");
            var Q48;
            Q48=sQuery(id+"F4.wireOp",VERTEX,"E7.2.7.0.center");
            var Q49;
            Q49=sQuery(id+"F4.wireOp",VERTEX,"E7.0.15.0.center");
            var Q50;
            Q50=sQuery(id+"F4.wireOp",VERTEX,"E7.1.11.0.center");
            var Q51;
            Q51=sQuery(id+"F4.wireOp",VERTEX,"E7.2.6.0.center");
            var Q52;
            Q52=sQuery(id+"F4.wireOp",VERTEX,"E7.0.14.0.center");
            var Q53;
            Q53=sQuery(id+"F4.wireOp",VERTEX,"E7.1.10.0.center");
            var Q54;
            Q54=sQuery(id+"F4.wireOp",VERTEX,"E7.2.9.0.center");
            var Q55;
            Q55=sQuery(id+"F4.wireOp",VERTEX,"E7.0.17.0.center");
            var Q56;
            Q56=sQuery(id+"F4.wireOp",VERTEX,"E7.1.13.0.center");
            var Q57;
            Q57=sQuery(id+"F4.wireOp",VERTEX,"E7.2.8.0.center");
            var Q58;
            Q58=sQuery(id+"F4.wireOp",VERTEX,"E7.0.16.0.center");
            var Q59;
            Q59=sQuery(id+"F4.wireOp",VERTEX,"E7.1.12.0.center");
            var Q60;
            Q60=makeQuery(id+"F1.opExtrude","SWEPT_BODY",BODY,{"disambiguationData":[OSD([sQuery(id+"F0.wireOp",EDGE,"E0.bottom"),sQuery(id+"F0.wireOp",EDGE,"E0.top"),sQuery(id+"F0.wireOp",EDGE,"E0.left"),sQuery(id+"F0.wireOp",EDGE,"E0.right"),sQuery(id+"F0.wireOp",EDGE,"E1.bottom"),sQuery(id+"F0.wireOp",EDGE,"E1.top"),sQuery(id+"F0.wireOp",EDGE,"E1.left"),sQuery(id+"F0.wireOp",EDGE,"E1.right")])]});
            hole(context, id + "F5", {"style" : HoleStyle.SIMPLE, "endStyle" : HoleEndStyle.THROUGH, "holeDiameter" : 5.1 * mm, "isTappedThrough" : true, "tappedDepth" : 12.7 * mm, "tapClearance" : 3, "locations" : qUnion([Q0, Q1, Q2, Q3, Q4, Q5, Q6, Q7, Q8, Q9, Q10, Q11, Q12, Q13, Q14, Q15, Q16, Q17, Q18, Q19, Q20, Q21, Q22, Q23, Q24, Q25, Q26, Q27, Q28, Q29, Q30, Q31, Q32, Q33, Q34, Q35, Q36, Q37, Q38, Q39, Q40, Q41, Q42, Q43, Q44, Q45, Q46, Q47, Q48, Q49, Q50, Q51, Q52, Q53, Q54, Q55, Q56, Q57, Q58, Q59]), "scope" : qUnion([Q60])});
        }
    });
